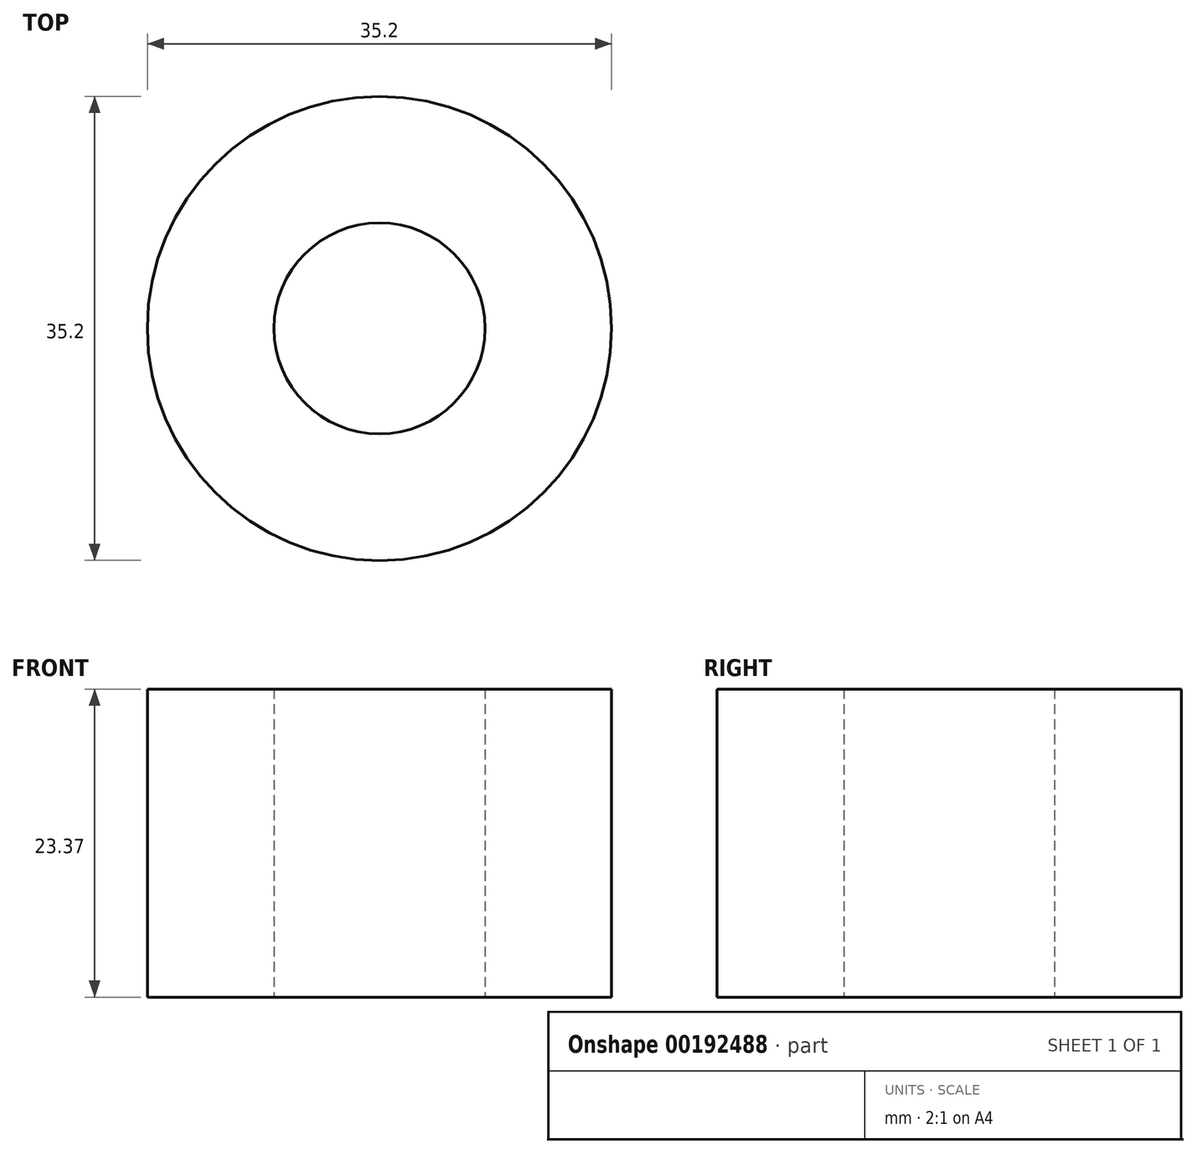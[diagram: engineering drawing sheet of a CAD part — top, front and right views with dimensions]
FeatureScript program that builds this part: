
annotation { "Feature Type Name" : "Feature", "Feature Type Description" : "" }
export const myFeature = defineFeature(function(context is Context, id is Id, definition is map)
    precondition{}
    {
        {
            var Q0;
            Q0=qCreatedBy(makeId("Top.planeOp"),FACE);
            var sketch = newSketch(context, id + "F0", { "sketchPlane" : qUnion([Q0])});
            skCircle(sketch, "E0", {"center": v(0, 0) * mm, "radius": 17.6 * mm});
            skCircle(sketch, "E1", {"center": v(0, 0) * mm, "radius": 8 * mm});
            skSolve(sketch);
        }
        {
            var Q0;
            Q0 = qSketchRegion(id + "F0", true);
            extrude(context, id + "F1", {"entities" : qUnion([Q0]), "depth" : 23.37 * mm});
        }
    });
